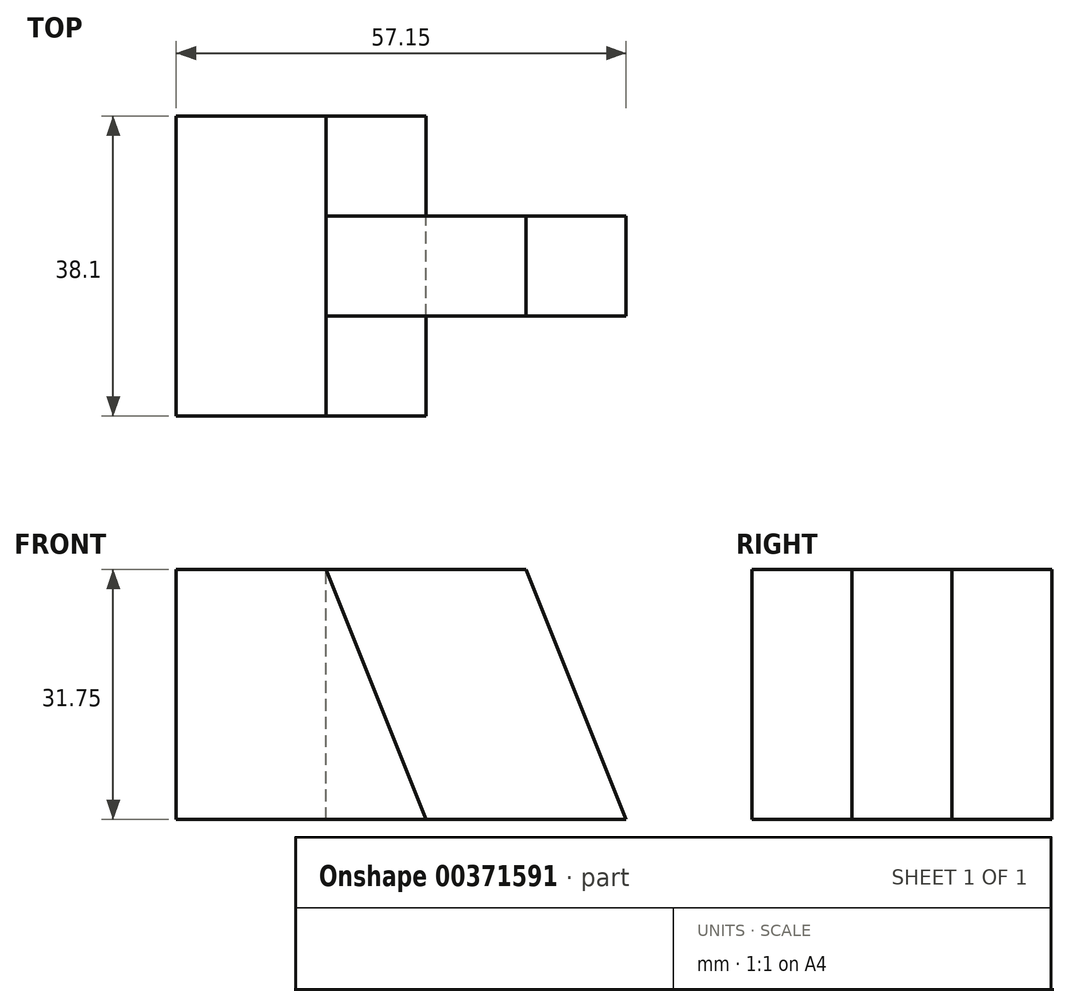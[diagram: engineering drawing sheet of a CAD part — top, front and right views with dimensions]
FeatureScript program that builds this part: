
annotation { "Feature Type Name" : "Feature", "Feature Type Description" : "" }
export const myFeature = defineFeature(function(context is Context, id is Id, definition is map)
    precondition{}
    {
        {
            var Q0;
            Q0=qCreatedBy(makeId("Front.planeOp"),FACE);
            var sketch = newSketch(context, id + "F0", { "sketchPlane" : qUnion([Q0])});
            skLineSegment(sketch, "E0", {"start": v(0, 0) * mm, "end": v(-31.75, 0) * mm});
            skLineSegment(sketch, "E1", {"start": v(-31.75, 0) * mm, "end": v(-31.75, 31.75) * mm});
            skLineSegment(sketch, "E2", {"start": v(-12.7, 31.75) * mm, "end": v(-31.75, 31.75) * mm});
            skLineSegment(sketch, "E3", {"start": v(-12.7, 31.75) * mm, "end": v(0, 0) * mm});
            skSolve(sketch);
        }
        {
            var Q0;
            Q0 = qSketchRegion(id + "F0", true);
            extrude(context, id + "F1", {"entities" : qUnion([Q0]), "depth" : 38.1 * mm});
        }
        {
            var Q0;
            Q0=makeQuery(id+"F1.opExtrude","SWEPT_FACE",FACE,{"disambiguationData":[OSD([sQuery(id+"F0.wireOp",EDGE,"E2")])]});
            var sketch = newSketch(context, id + "F2", { "sketchPlane" : qUnion([Q0])});
            skLineSegment(sketch, "E4", {"start": v(-12.7, -12.7) * mm, "end": v(12.7, -12.7) * mm});
            skLineSegment(sketch, "E5", {"start": v(12.7, -25.4) * mm, "end": v(-12.7, -25.4) * mm});
            skLineSegment(sketch, "E6", {"start": v(12.7, -12.7) * mm, "end": v(12.7, -25.4) * mm});
            skSolve(sketch);
        }
        {
            var Q0;
            {var subQ0=sQuery(id+"F2.wireOp",EDGE,"E4");Q0=makeQuery(id+"F2.imprint","IMPRINT",FACE,{"disambiguationData":[TD([[makeQuery(id+"F2.imprint","IMPRINT",EDGE,{"derivedFrom":subQ0}),-1.0]])]});}
            extrude(context, id + "F3", {"entities" : qUnion([Q0]), "oppositeDirection" : true, "depth" : 31.75 * mm});
        }
        {
            var Q0;
            Q0=makeQuery(id+"F3.opExtrude","SWEPT_FACE",FACE,{"disambiguationData":[OSD([sQuery(id+"F2.wireOp",EDGE,"E5")])]});
            var sketch = newSketch(context, id + "F4", { "sketchPlane" : qUnion([Q0])});
            skLineSegment(sketch, "E7", {"start": v(12.7, 31.75) * mm, "end": v(25.4, 0) * mm});
            skLineSegment(sketch, "E8", {"start": v(25.4, 0) * mm, "end": v(12.7, 0) * mm});
            skSolve(sketch);
        }
        {
            var Q0;
            Q0=makeQuery(id+"F4.imprint","IMPRINT",FACE,{"disambiguationData":[TD([[makeQuery(id+"F4.imprint","IMPRINT",EDGE,{"derivedFrom":sQuery(id+"F4.wireOp",EDGE,"E7")}),-1.0]])]});
            extrude(context, id + "F5", {"entities" : qUnion([Q0]), "operationType" : NewBodyOperationType.ADD, "oppositeDirection" : true, "depth" : 12.7 * mm});
        }
    });
